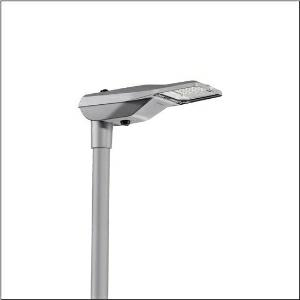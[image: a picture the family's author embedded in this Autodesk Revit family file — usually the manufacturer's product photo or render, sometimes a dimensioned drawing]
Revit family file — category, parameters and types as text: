
# Revit family: streetlight_sl_21_micro___st0_8a_5xe1c33t08db_e381
name_source: partatom
category: Lighting Fixtures
units: mm (PartAtom-declared; Revit-internal decimal feet)

## family parameters
Cut with Voids When Loaded = No
Host = Face
Light Source = No
Part Type = Normal
Room Calculation Point = No
Round Connector Dimension = Use Diameter
Shared = No

## types (1)
- --- (1 x LED, 5110 lm, 39.1 W, 3000K)
    Apparent Load = 39 VA
    CIE Flux Codes = 38 75 97 100 100
    Color Rendering = 70
    Color Temperature = 3000K
    Default Elevation = 1800 mm
    Description = Streetlight SL 21 micro, mast luminaire, primary light control with lens, of PMMA, primary optical cover: cover, of toughened safety glass, transparent, light distribution: ST0.8a, light emission: direct distribution, primary light characteristic: asymmetric, installation type: side-entry, post-top, LED, High Power LED, rated luminous flux: 5.110lm, luminous efficacy: 131lm/W, light colour: 730, colour temperature: 3000K, control gear: D4i, control: flexible luminous flux parameterisation, time-dependent luminous flux control, constant luminous flux control, overheat protection, pre-setting: logarithmic dimming characteristic, mains connection: 220..240V, AC, 50/60Hz, start of lifetime: 39W, end of service life: 41W, reduction: 18W, luminaire housing, of diecast aluminium, powder-coated, Siteco® metallic grey (DB 702S), corrosivity category C5 mid according to DIN EN ISO 12944, please order mast flange separately, inclination adjustable: 0°, 5°, 10°, 15°, sealing non-destructively replaceable, multi-level sealing system, length: 528mm, width: 235mm, height: 110mm, mast flange for spigot size: 42mm (side-entry): 5XC10008XM4, 60/48mm (side-entry/post-top): 5XC10108XM2, 76/60mm (side-entry/post-top): 5XC10108XM1, Smart Interface below and above, protection rating (complete): IP66, insulation class (complete): insulation class II (safety insulation), certification: CE, ENEC, ENEC+, VDE, impact resistance: IK10, permissible operating ambient temperature for outdoor applications: -40..+50°C, standard-compliant lighting for roads and squares, packaging unit: 1 piece

Light Distribution: ST0.8a
    Height = 110 mm
    Lamp = 1 x LED
    Lamp Light Flux = 5110 lm
    Lamp Power = 39.1 W
    Lamp count = 1
    Length = 528 mm
    Luminous efficacy = 131 lm/W
    Manufacturer = Siteco
    ModVariant = No
    Model = 5XE1C33T08DB
    Number of Poles = 1
    OnlyDefault = Yes
    Power Factor = 1
    Product Name = Streetlight SL 21 micro | ST0.8a
    Product group = mast luminaire | pylon top
    ProductGroupID = 6100
    Protection Class = Protection class II
    Protection Degree = IP 66
    RLX_Detail_Level = 1
    RLX_Emergency_Light_Flux = 0 lm
    RLX_Emergency_Type = 0
    RLX_Emergency_Type_DB = No
    RlxData = <blob elided: 98241 chars, md5=4cabec0f>
    Socket = socket
    Standby Power = 0 W
    System Light Flux = 5110 lm
    System Power = 39 W
    Type Comments = factory setting: luminous flux: 100 % | dim-lin: 254 | 765 mA
    Type Image = l_1007239.jpg
    URL = http://relux.com
    VarID = @adj_154390
    Voltage = 0 V
    Weight = 0.00 kg
    Width = 235 mm

## geometry (parser evidence)
native form markers: Blend x4, Sweep x10
no freeform markers — native parametric forms only
